# Revit family: Palissade Chair
name_source: partatom
category: Furniture
revit_build: Autodesk Revit 2016 (Build: 20161004_0715(x64)
units: mm (PartAtom-declared; Revit-internal decimal feet)

## family parameters
Always vertical = Yes
Cut with Voids When Loaded = No
OmniClass Number = 23.40.20.00
OmniClass Title = General Furniture and Specialties
Room Calculation Point = No
Shared = No
Work Plane-Based = No

## types (1)
- Palissade Chair
    Base = HAY Anthracite powder coated steel
    Depth = 56cm - 22.05inch
    Description = Versatile and elegant outdoor chair in tubular steel with slatted design. Suitable for cafés, restaurants, gardens, terraces and balconies.
    Design = Ronan & Erwan Bouroullec
    Gliders = HAY Standard Gliders
    Height = 80cm - 31.5inch
    Manufacturer = HAY
    Model = Palissade Chair
    Price = Contact HAY or visit hay.dk
    Seat Height = 45cm - 17.72inch
    Strength, durability and safety = EN 581-2:2009, EN 1022:2005, EN 16139:2013 L2
    Type Comments = Multifunctional outdoor furniture collection comprising chairs, benches, stools, lounges, sofas and tables.
    URL = https://hay.dk
    Variations = Different colour options in powder coated steel. Can be supplemented with seat cushions.
    Width = 47cm - 18.5inch

## geometry (parser evidence)
native form markers: Sweep x2
no freeform markers — native parametric forms only
